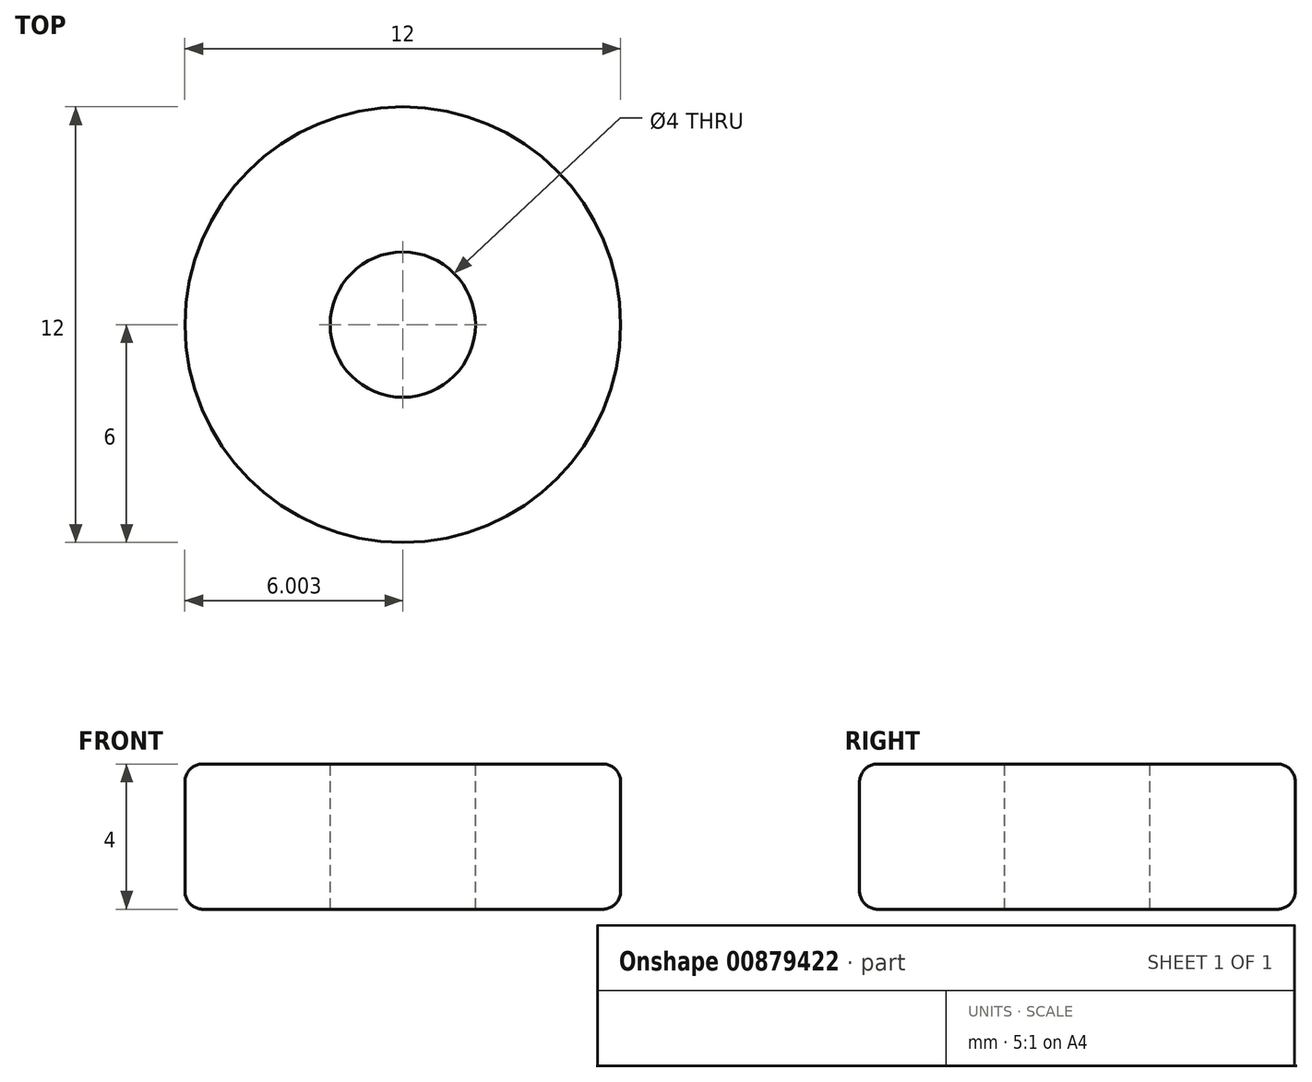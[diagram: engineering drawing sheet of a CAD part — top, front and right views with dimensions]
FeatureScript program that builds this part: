
annotation { "Feature Type Name" : "Feature", "Feature Type Description" : "" }
export const myFeature = defineFeature(function(context is Context, id is Id, definition is map)
    precondition{}
    {
        {
            var Q0;
            Q0=qCreatedBy(makeId("Top.planeOp"),FACE);
            var sketch = newSketch(context, id + "F0", { "sketchPlane" : qUnion([Q0])});
            skCircle(sketch, "E0", {"center": v(-26.95, 0) * mm, "radius": 6 * mm});
            skSolve(sketch);
        }
        {
            var Q0;
            Q0=qSketchRegion(id+"F0",true);
            extrude(context, id + "F1", {"entities" : qUnion([Q0]), "depth" : 4 * mm});
        }
        {
            var Q0;
            Q0=makeQuery(id+"F1.opExtrude","CAP_FACE",FACE,{"disambiguationData":[OSD([sQuery(id+"F0.wireOp",EDGE,"E0")])],"isStart":false});
            var sketch = newSketch(context, id + "F2", { "sketchPlane" : qUnion([Q0])});
            skCircle(sketch, "E1", {"center": v(-26.95, 0) * mm, "radius": 2 * mm});
            skSolve(sketch);
        }
        {
            var Q0;
            Q0=qSketchRegion(id+"F2",true);
            extrude(context, id + "F3", {"entities" : qUnion([Q0]), "operationType" : NewBodyOperationType.REMOVE, "endBound" : BoundingType.THROUGH_ALL, "oppositeDirection" : true, "depth" : 25 * mm});
        }
        {
            var Q0;
            Q0=makeQuery(id+"F1.opExtrude","CAP_EDGE",EDGE,{"disambiguationData":[OSD([sQuery(id+"F0.wireOp",EDGE,"E0")])],"isStart":true});
            var Q1;
            Q1=makeQuery(id+"F1.opExtrude","CAP_EDGE",EDGE,{"disambiguationData":[OSD([sQuery(id+"F0.wireOp",EDGE,"E0")])],"isStart":false});
            fillet(context, id + "F4", {"entities" : qUnion([Q0, Q1]), "radius" : .5 * mm, "tangentPropagation" : true, "allowEdgeOverflow" : false});
        }
    });
